# Revit family: Gripple Standard Hanger with Universal Clamp and M8 Adaptor - Assembly
name_source: partatom
category: Specialty Equipment
revit_build: Autodesk Revit 2017 (Build: 20160606_1515(x64)
units: mm (PartAtom-declared; Revit-internal decimal feet)

## family parameters
Always vertical = Yes
Cut with Voids When Loaded = No
Part Type = Normal
Room Calculation Point = No
Round Connector Dimension = Use Diameter
Shared = Yes
Work Plane-Based = Yes

## types (4) — shared parameters
D = 6 mm  [stored 0.019685 ft]
Gripple Length = 45 mm  [stored 0.147638 ft]
Gripple Width = 25 mm  [stored 0.082021 ft]
Half Angle = 5.00°
Included Angle = 10.00°
Loop Centre = 80 mm  [stored 0.262467 ft]
Manufacturer = Gripple Ltd
T = 7 mm  [stored 0.0229659 ft]
T/2 = 4 mm  [stored 0.0131234 ft]
T/2 (-) = -4 mm
Triangle h = 44 mm
Wire Entry Triangle Top Distance = 23 mm
zero-valued in all types: Default Elevation

## per-type parameters (varying)
| type | Assembly Code | Model | WireRadius |
| GUC400 c/w HF2 | GUC400, HF2 | GUC 400mm w/ Standard Hanger No2 | 1 mm  [stored 0.00328084 ft] |
| GUC600 c/w HF2 | GUC600, HF2 | GUC 600mm w/ Standard Hanger No2 | 1 mm  [stored 0.00328084 ft] |
| GUC400 c/w HF3 | GUC400, HF3 | GUC 400mm w/ Standard Hanger No3 | 2 mm  [stored 0.00656168 ft] |
| GUC600 c/w HF3 | GUC600, HF3 | GUC 600mm w/ Standard Hanger No3 | 2 mm  [stored 0.00656168 ft] |

note: [stored X ft] marks values corroborated as IEEE doubles in the binary element streams (Revit-internal decimal feet)

## geometry (parser evidence)
native form markers: Blend x2, Sweep x6
no freeform markers — native parametric forms only
